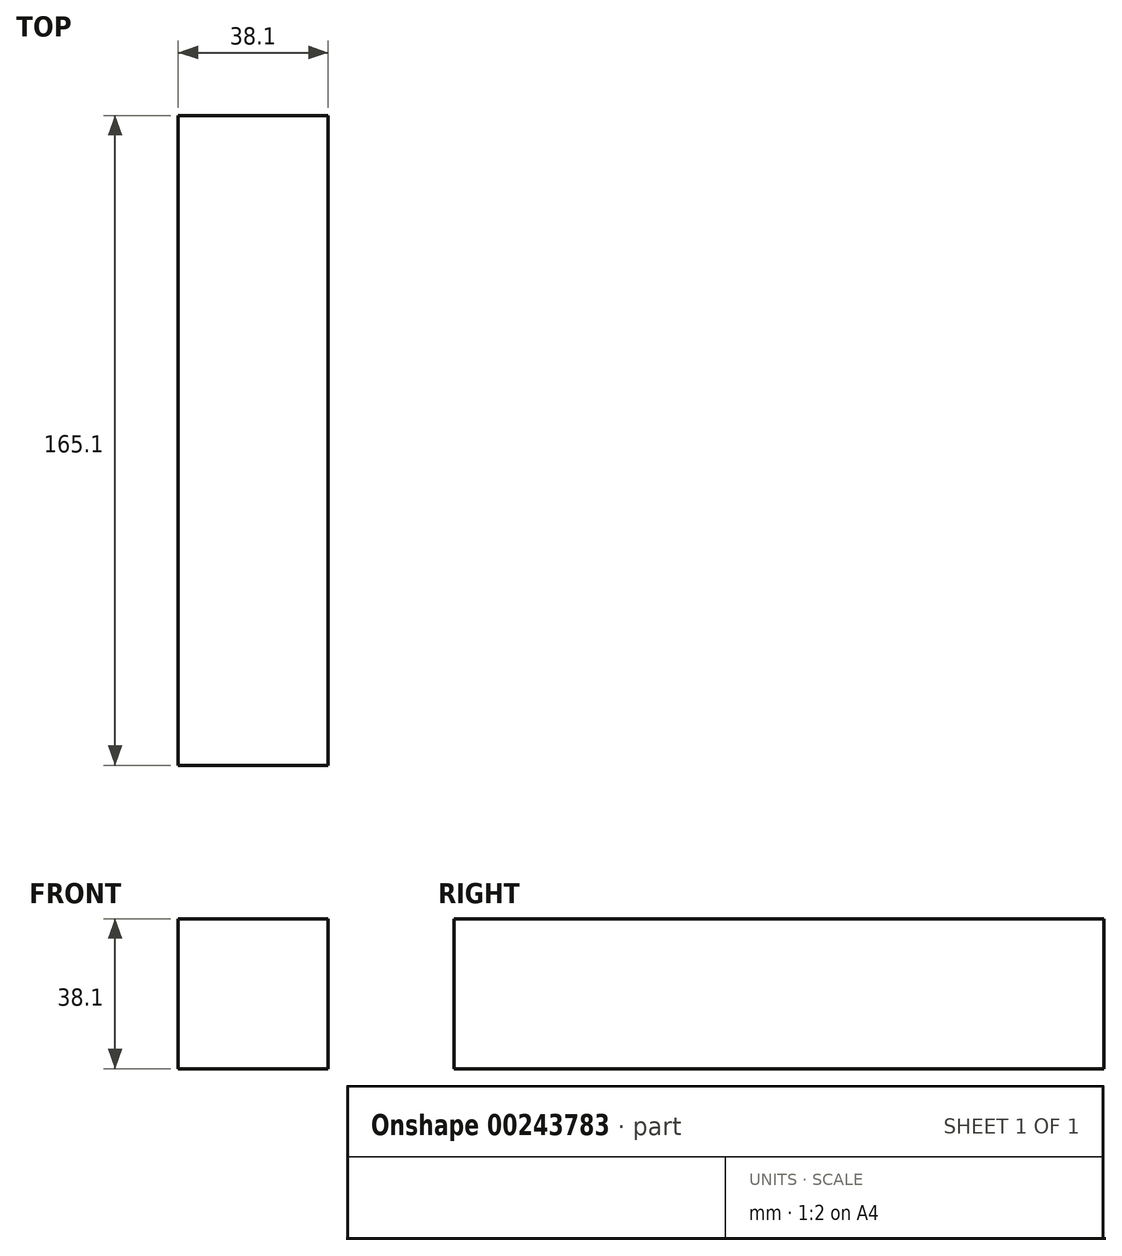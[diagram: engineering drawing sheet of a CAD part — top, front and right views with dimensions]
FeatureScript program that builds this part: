
annotation { "Feature Type Name" : "Feature", "Feature Type Description" : "" }
export const myFeature = defineFeature(function(context is Context, id is Id, definition is map)
    precondition{}
    {
        {
            var Q0;
            Q0=qCreatedBy(makeId("Front.planeOp"),FACE);
            var sketch = newSketch(context, id + "F0", { "sketchPlane" : qUnion([Q0])});
            skLineSegment(sketch, "E0.bottom", {"start": v(-16.22, 28.36) * mm, "end": v(21.88, 28.36) * mm});
            skLineSegment(sketch, "E0.top", {"start": v(-16.22, -9.74) * mm, "end": v(21.88, -9.74) * mm});
            skLineSegment(sketch, "E0.left", {"start": v(-16.22, 28.36) * mm, "end": v(-16.22, -9.74) * mm});
            skLineSegment(sketch, "E0.right", {"start": v(21.88, 28.36) * mm, "end": v(21.88, -9.74) * mm});
            skSolve(sketch);
        }
        {
            var Q0;
            Q0=makeQuery(id+"F0.imprint","IMPRINT",FACE,{"disambiguationData":[TD([[makeQuery(id+"F0.imprint","IMPRINT",EDGE,{"derivedFrom":sQuery(id+"F0.wireOp",EDGE,"E0.bottom")}),-1.0]])]});
            extrude(context, id + "F1", {"entities" : qUnion([Q0]), "depth" : 165.1 * mm});
        }
    });
